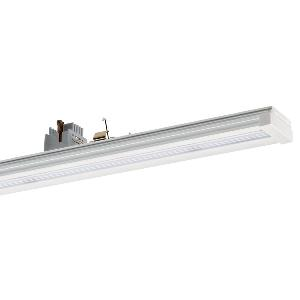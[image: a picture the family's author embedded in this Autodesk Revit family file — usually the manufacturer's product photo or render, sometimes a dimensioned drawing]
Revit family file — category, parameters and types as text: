
# Revit family: conveo_-_cvg_4500_840_xn-p_ea_5_226848199-00804957_bf1f
name_source: partatom
category: Lighting Fixtures
units: mm (PartAtom-declared; Revit-internal decimal feet)

## family parameters
Cut with Voids When Loaded = No
Host = Face
Light Source = No
Part Type = Normal
Room Calculation Point = No
Round Connector Dimension = Use Diameter
Shared = No

## types (1)
- CONVEO - CVG 4500/840/xN-P/EA/5 (1 x LED, 4200 lm, 4000K)
    Apparent Load = 28 VA
    Approval mark = CE
    CIE Flux Codes = 57 84 97 100 100
    Color Rendering = 80-89
    Color Temperature = 4000K
    Control Gear = Electronic ballast
    Default Elevation = 1800 mm
    Description = CVG 4500/840/xN-P/EA/5|Continuous-row system|light source: LED|work equipment: Electronic ballast|connected load: 220-240 V, 50-60 Hz|Power consumption: approx. 28 W|luminous flux: 4200 lm|luminous efficacy: 150 lm/W|colour temperature: Cold white, ca. 4000 K|color rendering index (CRI): >= 80|chromaticity tolerance:  3 SDCM|System of protection: IP 54|class of protection: I|technology: Switchable|luminaire body|material: Aluminium|surface: Powder coatet|colour: White|lamp cover: Acrylic (PMMA), Satine|weight (net): approx. 1.9 kg|Fastening: Available separately|minimum ambient temperature: -25 ░C|maximum ambient temperature: 56 ░C|glare control: Prism optics (linear)|Approval mark: VDE - ENEC|
    Frequency = 50 Hz
    Height = 70 mm
    Lamp = 1 x LED
    Lamp Light Flux = 4200 lm
    Lamp count = 1
    Length = 1500 mm
    Luminous efficacy = 150 lm/W
    Manufacturer = Waldmann
    ModVariant = No
    Model = 226848199-00804957
    Mounting Place = Ceiling
    Mounting Type = Pendant
    Number of Poles = 1
    OnlyDefault = Yes
    Power Factor = 1
    Product Name = CONVEO - CVG 4500/840/xN-P/EA/5
    Product group = Continuous-row system (industry)
    ProductGroupID = 301
    Protection Class = Protection class I
    Protection Degree = IP 54
    RLX_Detail_Level = 1
    RlxData = <blob elided: 100173 chars, md5=ef768486>
    Socket = socket
    Standby Power = 0 W
    System Light Flux = 4200 lm
    System Power = 28 W
    Type Comments = Product without accessories
    Type Image = 226848079-00804943-1p5.jpg
    URL = http://relux.com
    VarID = ---
    Voltage = 230 V
    Voltage Range = 220-240 V
    Weight = 0.00 kg
    Width = 64 mm

## geometry (parser evidence)
native form markers: Blend x4, Sweep x11
no freeform markers — native parametric forms only
